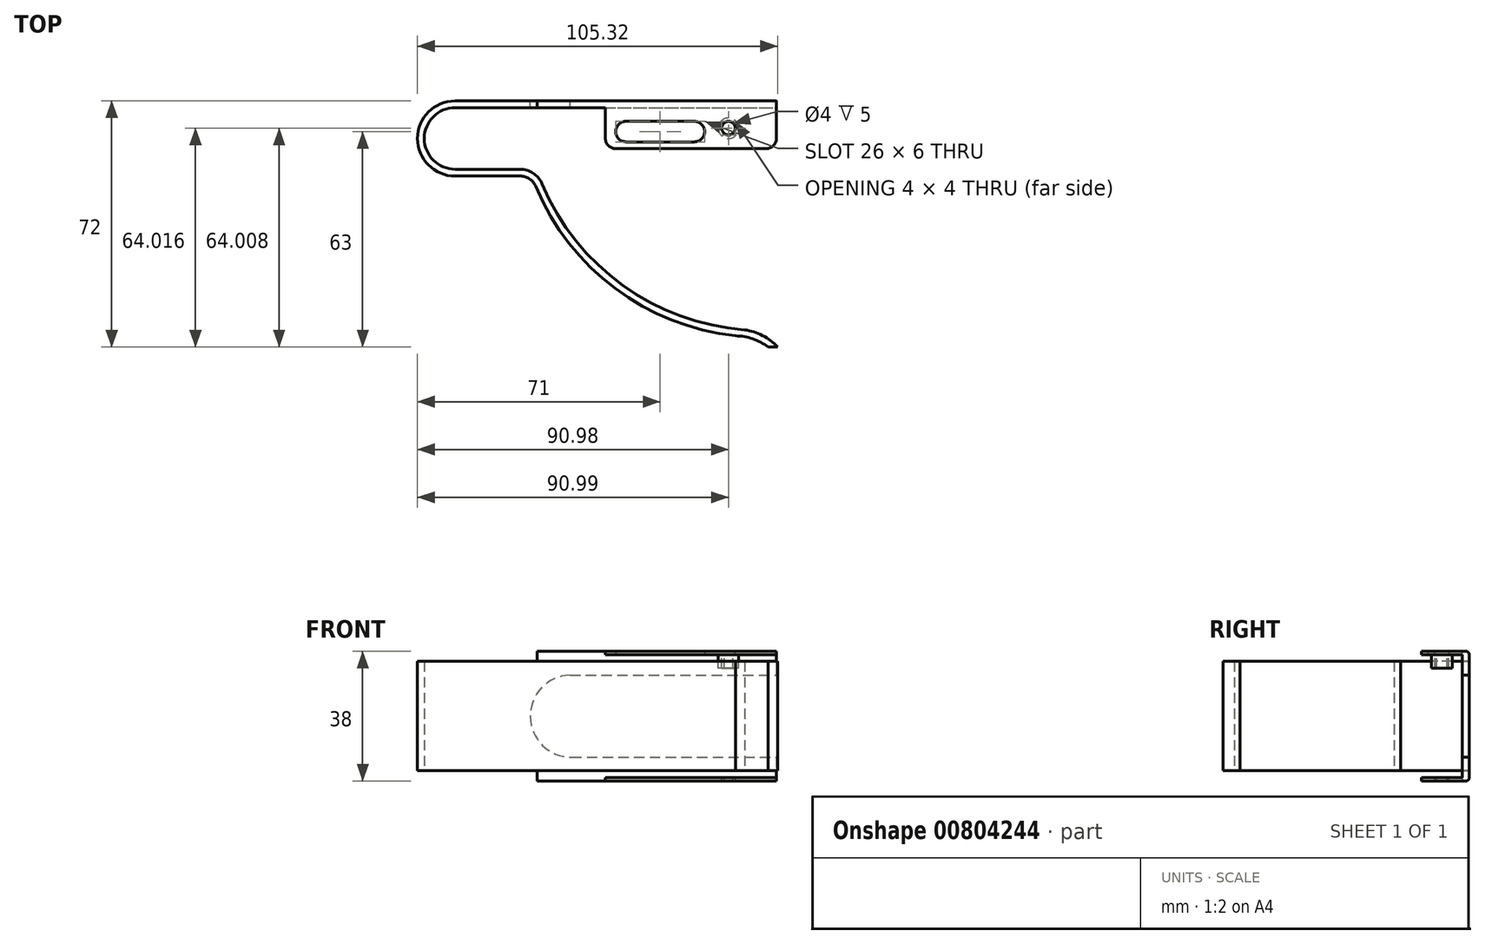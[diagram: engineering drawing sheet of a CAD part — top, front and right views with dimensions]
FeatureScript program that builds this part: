
annotation { "Feature Type Name" : "Feature", "Feature Type Description" : "" }
export const myFeature = defineFeature(function(context is Context, id is Id, definition is map)
    precondition{}
    {
        {
            var Q0;
            Q0=qCreatedBy(makeId("Top.planeOp"),FACE);
            var sketch = newSketch(context, id + "F0", { "sketchPlane" : qUnion([Q0])});
            skArc(sketch, "E0", {"start": v(0, 11) * mm, "mid": v(-11, 0) * mm, "end": v(0, -11) * mm});
            skLineSegment(sketch, "E1", {"start": v(0, 11) * mm, "end": v(94, 11) * mm});
            skLineSegment(sketch, "E2", {"start": v(0, -11) * mm, "end": v(19, -11) * mm});
            skArc(sketch, "E3", {"start": v(23.61, -14.06) * mm, "mid": v(46.86, -43.85) * mm, "end": v(82, -57.75) * mm});
            skPoint(sketch, "E4.visualSharp", {"position": v(22.4, -11) * mm});
            skArc(sketch, "E4.filletArc", {"start": v(23.61, -14.06) * mm, "mid": v(21.77, -11.84) * mm, "end": v(19, -11) * mm});
            skLineSegment(sketch, "E5.0", {"start": v(0, 9) * mm, "end": v(94, 9) * mm});
            skArc(sketch, "E5.1", {"start": v(25.45, -13.3) * mm, "mid": v(49.07, -42.99) * mm, "end": v(84.7, -56) * mm});
            skArc(sketch, "E5.2", {"start": v(25.45, -13.3) * mm, "mid": v(22.88, -10.17) * mm, "end": v(19, -9) * mm});
            skLineSegment(sketch, "E5.3", {"start": v(0, -9) * mm, "end": v(19, -9) * mm});
            skArc(sketch, "E5.4", {"start": v(0, 9) * mm, "mid": v(-9, 0) * mm, "end": v(0, -9) * mm});
            skLineSegment(sketch, "E6", {"start": v(94, 11) * mm, "end": v(94, 9) * mm});
            skArc(sketch, "E7", {"start": v(91.6, -61) * mm, "mid": v(87.06, -58.6) * mm, "end": v(82, -57.75) * mm});
            skArc(sketch, "E8.0", {"start": v(94.32, -61) * mm, "mid": v(89.95, -57.66) * mm, "end": v(84.7, -56) * mm});
            skLineSegment(sketch, "E9", {"start": v(91.6, -61) * mm, "end": v(94.32, -61) * mm});
            skSolve(sketch);
        }
        {
            var Q0;
            Q0 = qSketchRegion(id + "F0", true);
            extrude(context, id + "F1", {"entities" : qUnion([Q0]), "depth" : 16 * mm, "offsetDistance" : 25 * mm});
        }
        {
            var Q0;
            Q0=makeQuery(id+"F1.opExtrude","SWEPT_FACE",FACE,{"disambiguationData":[OSD([sQuery(id+"F0.wireOp",EDGE,"E1")])]});
            var sketch = newSketch(context, id + "F2", { "sketchPlane" : qUnion([Q0])});
            skLineSegment(sketch, "E10.bottom", {"start": v(-94, 16) * mm, "end": v(-24, 16) * mm});
            skLineSegment(sketch, "E10.top", {"start": v(-94, 19) * mm, "end": v(-24, 19) * mm});
            skLineSegment(sketch, "E10.left", {"start": v(-94, 16) * mm, "end": v(-94, 19) * mm});
            skLineSegment(sketch, "E10.right", {"start": v(-24, 16) * mm, "end": v(-24, 19) * mm});
            skSolve(sketch);
        }
        {
            var Q0;
            Q0 = qSketchRegion(id + "F2", true);
            extrude(context, id + "F3", {"entities" : qUnion([Q0]), "operationType" : NewBodyOperationType.ADD, "oppositeDirection" : true, "depth" : 2 * mm, "offsetDistance" : 25 * mm});
        }
        {
            var Q0;
            Q0=makeQuery(id+"F3.opExtrude","SWEPT_FACE",FACE,{"disambiguationData":[OSD([sQuery(id+"F2.wireOp",EDGE,"E10.top")])]});
            var sketch = newSketch(context, id + "F4", { "sketchPlane" : qUnion([Q0])});
            skLineSegment(sketch, "E11.bottom", {"start": v(44, 11) * mm, "end": v(94, 11) * mm});
            skLineSegment(sketch, "E11.top", {"start": v(44, -3) * mm, "end": v(94, -3) * mm});
            skLineSegment(sketch, "E11.left", {"start": v(44, 11) * mm, "end": v(44, -3) * mm});
            skLineSegment(sketch, "E11.right", {"start": v(94, 11) * mm, "end": v(94, -3) * mm});
            skSolve(sketch);
        }
        {
            var Q0;
            Q0 = qSketchRegion(id + "F4", true);
            extrude(context, id + "F5", {"entities" : qUnion([Q0]), "operationType" : NewBodyOperationType.ADD, "oppositeDirection" : true, "depth" : 1 * mm, "offsetDistance" : 25 * mm});
        }
        {
            var Q0;
            Q0=makeQuery(id+"F5.opExtrude","CAP_EDGE",EDGE,{"disambiguationData":[OSD([sQuery(id+"F4.wireOp",EDGE,"E11.bottom")])],"isStart":false});
            var Q1;
            Q1=makeQuery(id+"F3.opExtrude","CAP_EDGE",EDGE,{"disambiguationData":[OSD([sQuery(id+"F2.wireOp",EDGE,"E10.top")])],"isStart":true});
            fillet(context, id + "F6", {"entities" : qUnion([Q0, Q1]), "radius" : 1 * mm, "tangentPropagation" : true, "allowEdgeOverflow" : false});
        }
        {
            var Q0;
            Q0=makeQuery(id+"F1.opExtrude","SWEPT_BODY",BODY,{"disambiguationData":[OSD([sQuery(id+"F0.wireOp",EDGE,"E0"),sQuery(id+"F0.wireOp",EDGE,"E1"),sQuery(id+"F0.wireOp",EDGE,"E2"),sQuery(id+"F0.wireOp",EDGE,"E3"),sQuery(id+"F0.wireOp",EDGE,"E4.filletArc"),sQuery(id+"F0.wireOp",EDGE,"E5.0"),sQuery(id+"F0.wireOp",EDGE,"E5.1"),sQuery(id+"F0.wireOp",EDGE,"E5.2"),sQuery(id+"F0.wireOp",EDGE,"E5.3"),sQuery(id+"F0.wireOp",EDGE,"E5.4"),sQuery(id+"F0.wireOp",EDGE,"E6"),sQuery(id+"F0.wireOp",EDGE,"E7"),sQuery(id+"F0.wireOp",EDGE,"E8.0"),sQuery(id+"F0.wireOp",EDGE,"E9")])]});
            var Q1;
            Q1=makeQuery(id+"F1.opExtrude","CAP_FACE",FACE,{"disambiguationData":[OSD([sQuery(id+"F0.wireOp",EDGE,"E0"),sQuery(id+"F0.wireOp",EDGE,"E1"),sQuery(id+"F0.wireOp",EDGE,"E2"),sQuery(id+"F0.wireOp",EDGE,"E3"),sQuery(id+"F0.wireOp",EDGE,"E4.filletArc"),sQuery(id+"F0.wireOp",EDGE,"E5.0"),sQuery(id+"F0.wireOp",EDGE,"E5.1"),sQuery(id+"F0.wireOp",EDGE,"E5.2"),sQuery(id+"F0.wireOp",EDGE,"E5.3"),sQuery(id+"F0.wireOp",EDGE,"E5.4"),sQuery(id+"F0.wireOp",EDGE,"E6"),sQuery(id+"F0.wireOp",EDGE,"E7"),sQuery(id+"F0.wireOp",EDGE,"E8.0"),sQuery(id+"F0.wireOp",EDGE,"E9")])],"isStart":true});
            mirror(context, id + "F7", {"operationType" : NewBodyOperationType.ADD, "entities" : qUnion([Q0]), "mirrorPlane" : qUnion([Q1])});
        }
        {
            var Q0;
            {var subQ0=makeQuery(id+"F3.boolean.opBoolean","MERGE",FACE,{"derivedFrom":[makeQuery(id+"F1.opExtrude","SWEPT_FACE",FACE,{"disambiguationData":[OSD([sQuery(id+"F0.wireOp",EDGE,"E1")])]}),makeQuery(id+"F3.opExtrude","CAP_FACE",FACE,{"disambiguationData":[OSD([sQuery(id+"F2.wireOp",EDGE,"E10.bottom"),sQuery(id+"F2.wireOp",EDGE,"E10.top"),sQuery(id+"F2.wireOp",EDGE,"E10.left"),sQuery(id+"F2.wireOp",EDGE,"E10.right")])],"isStart":true})]});Q0=makeQuery(id+"F7.boolean.opBoolean","MERGE",FACE,{"derivedFrom":[subQ0,makeQuery(id+"F7.opPattern","COPY",FACE,{"derivedFrom":subQ0,"instanceName":"1"})]});}
            var sketch = newSketch(context, id + "F8", { "sketchPlane" : qUnion([Q0])});
            skArc(sketch, "E12", {"start": v(-34, -12) * mm, "mid": v(-22, 0.16) * mm, "end": v(-34.33, 12) * mm});
            skLineSegment(sketch, "E13", {"start": v(-33.67, 12) * mm, "end": v(-94, 12) * mm});
            skLineSegment(sketch, "E14", {"start": v(-34, -12) * mm, "end": v(-94, -12) * mm});
            skSolve(sketch);
        }
        {
            var Q0;
            {var subQ0=sQuery(id+"F8.wireOp",EDGE,"E14");Q0=makeQuery(id+"F8.imprint","IMPRINT",FACE,{"disambiguationData":[TD([[makeQuery(id+"F8.imprint","IMPRINT",EDGE,{"derivedFrom":subQ0}),-1.0]])]});}
            extrude(context, id + "F9", {"entities" : qUnion([Q0]), "operationType" : NewBodyOperationType.REMOVE, "oppositeDirection" : true, "depth" : 2 * mm, "offsetDistance" : 25 * mm});
        }
        {
            var Q0;
            Q0=makeQuery(id+"F5.opExtrude","CAP_FACE",FACE,{"disambiguationData":[OSD([sQuery(id+"F4.wireOp",EDGE,"E11.bottom"),sQuery(id+"F4.wireOp",EDGE,"E11.top"),sQuery(id+"F4.wireOp",EDGE,"E11.left"),sQuery(id+"F4.wireOp",EDGE,"E11.right")])],"isStart":false});
            var sketch = newSketch(context, id + "F10", { "sketchPlane" : qUnion([Q0])});
            skLineSegment(sketch, "E15", {"start": v(50, -2) * mm, "end": v(70, -2) * mm});
            skArc(sketch, "E16.0.startCap", {"start": v(50, -5) * mm, "mid": v(47, -2) * mm, "end": v(50, 1) * mm});
            skArc(sketch, "E16.0.endCap", {"start": v(70, 1) * mm, "mid": v(73, -2) * mm, "end": v(70, -5) * mm});
            skLineSegment(sketch, "E16.0.left", {"start": v(50, 1) * mm, "end": v(70, 1) * mm});
            skLineSegment(sketch, "E16.0.right", {"start": v(50, -5) * mm, "end": v(70, -5) * mm});
            skSolve(sketch);
        }
        {
            var Q0;
            Q0 = qSketchRegion(id + "F10", true);
            extrude(context, id + "F11", {"entities" : qUnion([Q0]), "operationType" : NewBodyOperationType.REMOVE, "endBound" : BoundingType.THROUGH_ALL, "oppositeDirection" : true, "depth" : 54.8 * mm, "offsetDistance" : 25 * mm});
        }
        {
            var Q0;
            Q0=makeQuery(id+"F5.opExtrude","CAP_FACE",FACE,{"disambiguationData":[OSD([sQuery(id+"F4.wireOp",EDGE,"E11.bottom"),sQuery(id+"F4.wireOp",EDGE,"E11.top"),sQuery(id+"F4.wireOp",EDGE,"E11.left"),sQuery(id+"F4.wireOp",EDGE,"E11.right")])],"isStart":false});
            var sketch = newSketch(context, id + "F12", { "sketchPlane" : qUnion([Q0])});
            skPoint(sketch, "E17", {"position": v(80, -3) * mm});
            skSolve(sketch);
        }
        {
            var Q0;
            Q0=sQuery(id+"F12.wireOp",VERTEX,"E17");
            var Q1;
            Q1=makeQuery(id+"F1.opExtrude","SWEPT_BODY",BODY,{"disambiguationData":[OSD([sQuery(id+"F0.wireOp",EDGE,"E0"),sQuery(id+"F0.wireOp",EDGE,"E1"),sQuery(id+"F0.wireOp",EDGE,"E2"),sQuery(id+"F0.wireOp",EDGE,"E3"),sQuery(id+"F0.wireOp",EDGE,"E4.filletArc"),sQuery(id+"F0.wireOp",EDGE,"E5.0"),sQuery(id+"F0.wireOp",EDGE,"E5.1"),sQuery(id+"F0.wireOp",EDGE,"E5.2"),sQuery(id+"F0.wireOp",EDGE,"E5.3"),sQuery(id+"F0.wireOp",EDGE,"E5.4"),sQuery(id+"F0.wireOp",EDGE,"E6"),sQuery(id+"F0.wireOp",EDGE,"E7"),sQuery(id+"F0.wireOp",EDGE,"E8.0"),sQuery(id+"F0.wireOp",EDGE,"E9")])]});
            hole(context, id + "F13", {"style" : HoleStyle.SIMPLE, "endStyle" : HoleEndStyle.BLIND, "oppositeDirection" : true, "holeDiameter" : 4 * mm, "majorDiameter" : 5 * mm, "holeDepth" : 50 * mm, "isTappedThrough" : true, "tappedDepth" : 12 * mm, "tapClearance" : 3, "locations" : qUnion([Q0]), "scope" : qUnion([Q1])});
        }
        {
            var Q0;
            Q0=makeQuery(id+"F5.opExtrude","CAP_FACE",FACE,{"disambiguationData":[OSD([sQuery(id+"F4.wireOp",EDGE,"E11.bottom"),sQuery(id+"F4.wireOp",EDGE,"E11.top"),sQuery(id+"F4.wireOp",EDGE,"E11.left"),sQuery(id+"F4.wireOp",EDGE,"E11.right")])],"isStart":true});
            var sketch = newSketch(context, id + "F14", { "sketchPlane" : qUnion([Q0])});
            skCircle(sketch, "E18.0", {"center": v(80, 3) * mm, "radius": 2 * mm});
            skCircle(sketch, "E19.0", {"center": v(80, 3) * mm, "radius": 3 * mm});
            skSolve(sketch);
        }
        {
            var Q0;
            Q0 = qSketchRegion(id + "F14", true);
            extrude(context, id + "F15", {"entities" : qUnion([Q0]), "operationType" : NewBodyOperationType.ADD, "oppositeDirection" : true, "depth" : 5 * mm, "offsetDistance" : 25 * mm});
        }
        {
            var Q0;
            Q0=makeQuery(id+"F5.opExtrude","SWEPT_EDGE",EDGE,{"disambiguationData":[OSD([sQuery(id+"F4.wireOp",EDGE,"E11.top"),sQuery(id+"F4.wireOp",EDGE,"E11.right")])]});
            var Q1;
            Q1=makeQuery(id+"F5.opExtrude","SWEPT_EDGE",EDGE,{"disambiguationData":[OSD([sQuery(id+"F4.wireOp",EDGE,"E11.top"),sQuery(id+"F4.wireOp",EDGE,"E11.left")])]});
            var Q2;
            Q2=makeQuery(id+"F7.opPattern","COPY",EDGE,{"derivedFrom":makeQuery(id+"F5.opExtrude","SWEPT_EDGE",EDGE,{"disambiguationData":[OSD([sQuery(id+"F4.wireOp",EDGE,"E11.top"),sQuery(id+"F4.wireOp",EDGE,"E11.left")])]}),"instanceName":"1"});
            var Q3;
            Q3=makeQuery(id+"F7.opPattern","COPY",EDGE,{"derivedFrom":makeQuery(id+"F5.opExtrude","SWEPT_EDGE",EDGE,{"disambiguationData":[OSD([sQuery(id+"F4.wireOp",EDGE,"E11.top"),sQuery(id+"F4.wireOp",EDGE,"E11.right")])]}),"instanceName":"1"});
            fillet(context, id + "F16", {"entities" : qUnion([Q0, Q1, Q2, Q3]), "radius" : 3 * mm, "tangentPropagation" : true, "allowEdgeOverflow" : false});
        }
        {
            var Q0;
            Q0=makeQuery(id+"F5.boolean.opBoolean","MERGE",FACE,{"derivedFrom":[makeQuery(id+"F3.opExtrude","SWEPT_FACE",FACE,{"disambiguationData":[OSD([sQuery(id+"F2.wireOp",EDGE,"E10.top")])]}),makeQuery(id+"F5.opExtrude","CAP_FACE",FACE,{"disambiguationData":[OSD([sQuery(id+"F4.wireOp",EDGE,"E11.bottom"),sQuery(id+"F4.wireOp",EDGE,"E11.top"),sQuery(id+"F4.wireOp",EDGE,"E11.left"),sQuery(id+"F4.wireOp",EDGE,"E11.right")])],"isStart":true})]});
            var sketch = newSketch(context, id + "F17", { "sketchPlane" : qUnion([Q0])});
            skPoint(sketch, "E20", {"position": v(79.98, 3.02) * mm});
            skSolve(sketch);
        }
        {
            var Q0;
            Q0=sQuery(id+"F17.wireOp",VERTEX,"E20");
            var Q1;
            Q1=makeQuery(id+"F1.opExtrude","SWEPT_BODY",BODY,{"disambiguationData":[OSD([sQuery(id+"F0.wireOp",EDGE,"E0"),sQuery(id+"F0.wireOp",EDGE,"E1"),sQuery(id+"F0.wireOp",EDGE,"E2"),sQuery(id+"F0.wireOp",EDGE,"E3"),sQuery(id+"F0.wireOp",EDGE,"E4.filletArc"),sQuery(id+"F0.wireOp",EDGE,"E5.0"),sQuery(id+"F0.wireOp",EDGE,"E5.1"),sQuery(id+"F0.wireOp",EDGE,"E5.2"),sQuery(id+"F0.wireOp",EDGE,"E5.3"),sQuery(id+"F0.wireOp",EDGE,"E5.4"),sQuery(id+"F0.wireOp",EDGE,"E6"),sQuery(id+"F0.wireOp",EDGE,"E7"),sQuery(id+"F0.wireOp",EDGE,"E8.0"),sQuery(id+"F0.wireOp",EDGE,"E9")])]});
            hole(context, id + "F18", {"style" : HoleStyle.SIMPLE, "endStyle" : HoleEndStyle.BLIND, "holeDiameter" : 4 * mm, "majorDiameter" : 5 * mm, "holeDepth" : 50 * mm, "isTappedThrough" : true, "tappedDepth" : 12 * mm, "tapClearance" : 3, "locations" : qUnion([Q0]), "scope" : qUnion([Q1])});
        }
    });
